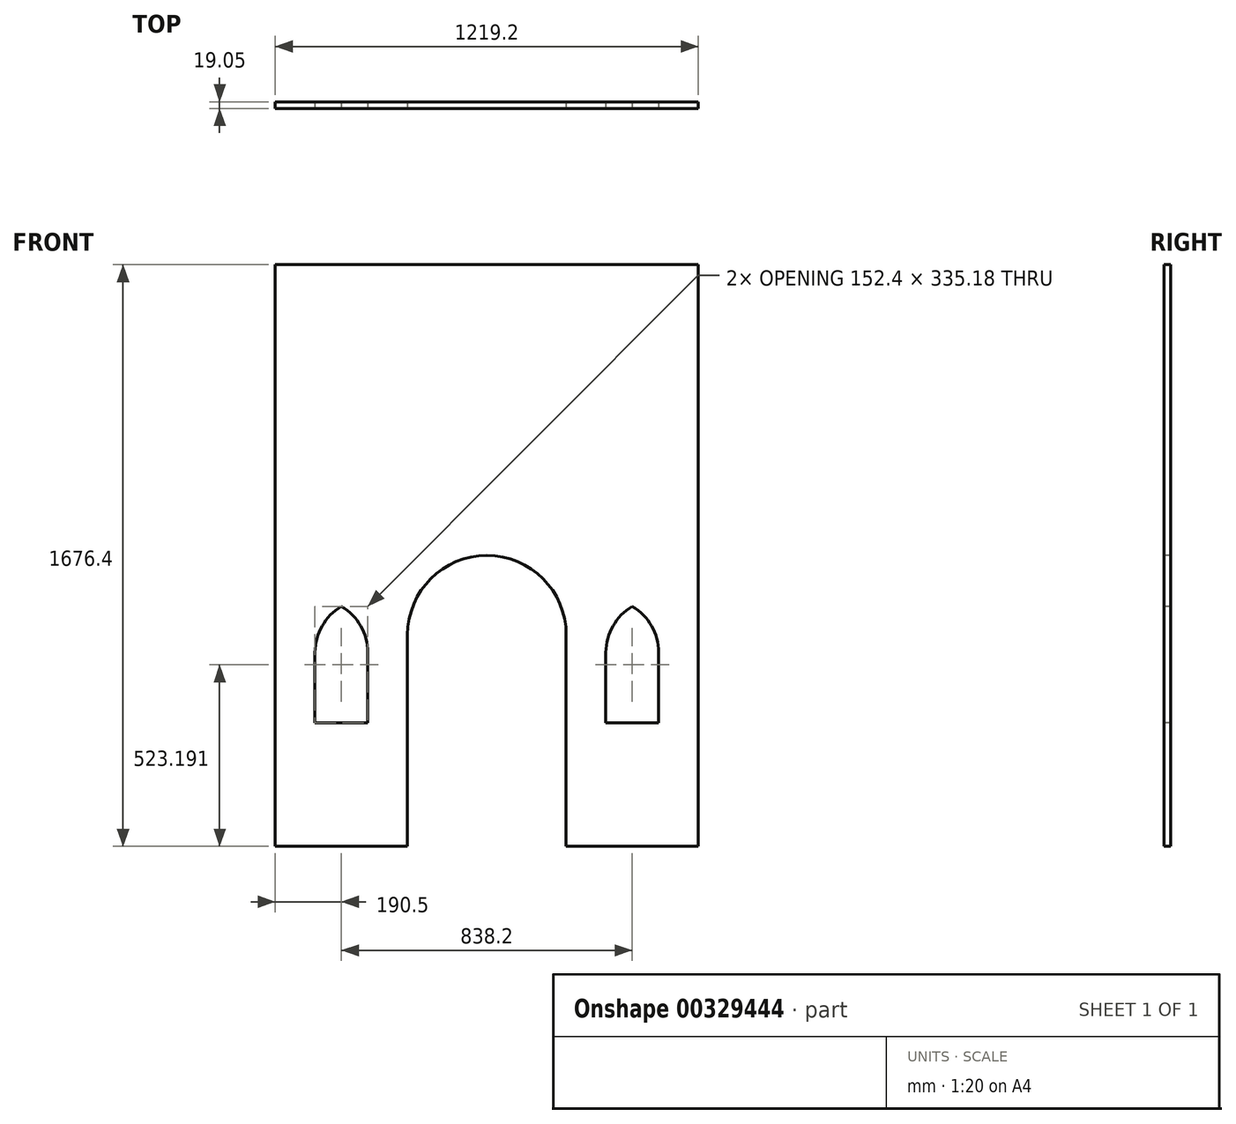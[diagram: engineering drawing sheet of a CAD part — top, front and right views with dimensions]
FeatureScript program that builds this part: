
annotation { "Feature Type Name" : "Feature", "Feature Type Description" : "" }
export const myFeature = defineFeature(function(context is Context, id is Id, definition is map)
    precondition{}
    {
        {
            var Q0;
            Q0=qCreatedBy(makeId("Front.planeOp"),FACE);
            var sketch = newSketch(context, id + "F0", { "sketchPlane" : qUnion([Q0])});
            skLineSegment(sketch, "E0.bottom", {"start": v(609.6, -838.2) * mm, "end": v(-609.6, -838.2) * mm});
            skLineSegment(sketch, "E0.top", {"start": v(609.6, 838.2) * mm, "end": v(-609.6, 838.2) * mm});
            skLineSegment(sketch, "E0.left", {"start": v(609.6, -838.2) * mm, "end": v(609.6, 838.2) * mm});
            skLineSegment(sketch, "E0.right", {"start": v(-609.6, -838.2) * mm, "end": v(-609.6, 838.2) * mm});
            skPoint(sketch, "E0.middle", {"position": v(0, 0) * mm});
            skSolve(sketch);
        }
        {
            var Q0;
            Q0 = qSketchRegion(id + "F0", true);
            extrude(context, id + "F1", {"entities" : qUnion([Q0]), "depth" : 19.05 * mm});
        }
        {
            var Q0;
            Q0=makeQuery(id+"F1.opExtrude","CAP_FACE",FACE,{"disambiguationData":[OSD([sQuery(id+"F0.wireOp",EDGE,"E0.bottom"),sQuery(id+"F0.wireOp",EDGE,"E0.top"),sQuery(id+"F0.wireOp",EDGE,"E0.left"),sQuery(id+"F0.wireOp",EDGE,"E0.right")])],"isStart":false});
            var sketch = newSketch(context, id + "F2", { "sketchPlane" : qUnion([Q0])});
            skLineSegment(sketch, "E1", {"start": v(0, 0) * mm, "end": v(0, -838.2) * mm, "construction": true});
            skLineSegment(sketch, "E2.bottom", {"start": v(-228.6, -838.2) * mm, "end": v(228.6, -838.2) * mm});
            skLineSegment(sketch, "E2.top", {"start": v(-228.6, -228.6) * mm, "end": v(228.6, -228.6) * mm, "construction": true});
            skLineSegment(sketch, "E2.left", {"start": v(-228.6, -838.2) * mm, "end": v(-228.6, -228.6) * mm});
            skLineSegment(sketch, "E2.right", {"start": v(228.6, -838.2) * mm, "end": v(228.6, -228.6) * mm});
            skArc(sketch, "E3", {"start": v(228.6, -228.6) * mm, "mid": v(0, 0) * mm, "end": v(-228.6, -228.6) * mm});
            skSolve(sketch);
        }
        {
            var Q0;
            Q0 = qSketchRegion(id + "F2", true);
            extrude(context, id + "F3", {"entities" : qUnion([Q0]), "operationType" : NewBodyOperationType.REMOVE, "endBound" : BoundingType.THROUGH_ALL, "oppositeDirection" : true, "depth" : 25.4 * mm});
        }
        {
            var Q0;
            Q0=makeQuery(id+"F1.opExtrude","CAP_FACE",FACE,{"disambiguationData":[OSD([sQuery(id+"F0.wireOp",EDGE,"E0.bottom"),sQuery(id+"F0.wireOp",EDGE,"E0.top"),sQuery(id+"F0.wireOp",EDGE,"E0.left"),sQuery(id+"F0.wireOp",EDGE,"E0.right")])],"isStart":false});
            var sketch = newSketch(context, id + "F4", { "sketchPlane" : qUnion([Q0])});
            skLineSegment(sketch, "E4", {"start": v(-609.6, -381) * mm, "end": v(-228.6, -381) * mm, "construction": true});
            skPoint(sketch, "E5", {"position": v(-419.1, -381) * mm});
            skLineSegment(sketch, "E6.bottom", {"start": v(-342.9, -482.6) * mm, "end": v(-495.3, -482.6) * mm});
            skLineSegment(sketch, "E6.top", {"start": v(-342.9, -279.4) * mm, "end": v(-495.3, -279.4) * mm, "construction": true});
            skLineSegment(sketch, "E6.left", {"start": v(-342.9, -482.6) * mm, "end": v(-342.9, -279.4) * mm});
            skLineSegment(sketch, "E6.right", {"start": v(-495.3, -482.6) * mm, "end": v(-495.3, -279.4) * mm});
            skLineSegment(sketch, "E7", {"start": v(-419.1, -381) * mm, "end": v(-419.1, 44.64) * mm, "construction": true});
            skArc(sketch, "E8", {"start": v(-419.1, -147.42) * mm, "mid": v(-474.88, -203.2) * mm, "end": v(-495.3, -279.4) * mm});
            skPoint(sketch, "E9", {"position": v(-419.1, -147.42) * mm});
            skArc(sketch, "E10.trimOffspring", {"start": v(-342.9, -279.4) * mm, "mid": v(-363.32, -203.2) * mm, "end": v(-419.1, -147.42) * mm});
            skPoint(sketch, "E11.MirrorP", {"position": v(419.1, -381) * mm});
            skArc(sketch, "E12.MirrorCS", {"start": v(342.9, -279.4) * mm, "mid": v(363.32, -203.2) * mm, "end": v(419.1, -147.42) * mm});
            skLineSegment(sketch, "E13.MirrorCS", {"start": v(342.9, -279.4) * mm, "end": v(495.3, -279.4) * mm, "construction": true});
            skLineSegment(sketch, "E14.MirrorCS", {"start": v(342.9, -482.6) * mm, "end": v(342.9, -279.4) * mm});
            skLineSegment(sketch, "E15.MirrorCS", {"start": v(342.9, -482.6) * mm, "end": v(495.3, -482.6) * mm});
            skPoint(sketch, "E16.MirrorP", {"position": v(419.1, -147.42) * mm});
            skArc(sketch, "E17.MirrorCS", {"start": v(419.1, -147.42) * mm, "mid": v(474.88, -203.2) * mm, "end": v(495.3, -279.4) * mm});
            skLineSegment(sketch, "E18.MirrorCS", {"start": v(495.3, -482.6) * mm, "end": v(495.3, -279.4) * mm});
            skSolve(sketch);
        }
        {
            var Q0;
            Q0 = qSketchRegion(id + "F4", true);
            extrude(context, id + "F5", {"entities" : qUnion([Q0]), "operationType" : NewBodyOperationType.REMOVE, "endBound" : BoundingType.THROUGH_ALL, "oppositeDirection" : true, "depth" : 25.4 * mm});
        }
    });
